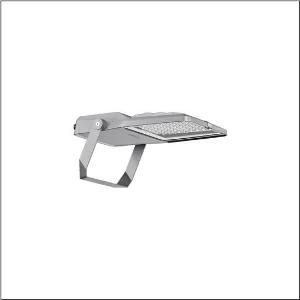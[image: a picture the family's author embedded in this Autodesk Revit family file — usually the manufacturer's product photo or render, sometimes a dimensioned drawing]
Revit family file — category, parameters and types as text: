
# Revit family: floodlight_fl_21_iq_mini___pl52_5xa7772c3d1a_c98d
name_source: partatom
category: Lighting Fixtures
units: mm (PartAtom-declared; Revit-internal decimal feet)

## family parameters
Cut with Voids When Loaded = No
Host = Face
Light Source = No
Part Type = Normal
Room Calculation Point = No
Round Connector Dimension = Use Diameter
Shared = No

## types (1)
- --- (1 x LED, 10510 lm, 87.2 W, 3000K)
    Apparent Load = 87 VA
    CIE Flux Codes = 26 60 98 100 100
    Color Rendering = 80
    Color Temperature = 3000K
    Default Elevation = 1800 mm
    Description = Floodlight FL 21 iQ mini, floodlight, primary light control with lens, of PMMA, primary optical cover: protective disc, of toughened safety glass, transparent, light distribution: PL52, light emission: direct distribution, installation type: surface-mounted, lamps: LED, High Power LED, rated values: 10.510lm | 87,2W | 120,5lm/W (begin service life); end service life: 10.510lm | 92,1W; at 50% lumin. flux: 5.255lm | 40,1W | 131lm/W, colour temperature: 3000K, colour rendering: CRI > 80, light colour: 830, light setting 1 begin service life: 100% | 10.510lm | 87,2W | 120,5lm/W | 3.000K, light setting 1 end service life: 92,1W, further light settings possible, control: Street-Remote, Auto-Match, Temp-Guard, Night-Set, Smart-Wire, Desk-Remote (wireless, voltage-free reading and setting of iQ features in the workshop via application-optimized NFC function/RFID function), optimised constant luminous flux control (CLO 2.0), pre-setting: linear dimming characteristic, with terminal, 6-pole, mains connection: 220..240V, AC, 50/60Hz, luminaire housing, of diecast aluminium, powder-coated, SITECO metallic grey (DB 702S), corrosivity category C5 mid according to DIN EN ISO 12944suitable for swimming poolschlorine-resistant, sealing non-destructively replaceable, mounting bracket, of steel, galvanised, powder-coated, SITECO metallic grey (DB 702S), protection rating (complete): IP66, insulation class (complete): insulation class II (safety insulation), certification: CE, ENEC, VDE, protection symbol: D, impact resistance: IK08, permissible operating ambient temperature: -40..+40°C, permissible operating ambient temperature for outdoor applications: -40..+50°C, standard: DIN EN 12944, LABS conformity tested according to VDMA 24364:2018-05, packaging unit: 1 piece

Light Distribution: PL52
    Height = 70 mm
    Lamp = 1 x LED
    Lamp Light Flux = 10510 lm
    Lamp Power = 87.2 W
    Lamp count = 1
    Length = 485 mm
    Luminous efficacy = 121 lm/W
    Manufacturer = Siteco
    ModVariant = No
    Model = 5XA7772C3D1A
    Mounting Place = Pole
    Mounting Type = Pole annexe
    Number of Poles = 1
    OnlyDefault = Yes
    Power Factor = 1
    Product Name = Floodlight FL 21 iQ mini | PL52
    Product group = floodlight | pylon annexe
    ProductGroupID = 6201
    Protection Class = Protection class II
    Protection Degree = IP 66
    RLX_Detail_Level = 1
    RLX_Emergency_Light_Flux = 0 lm
    RLX_Emergency_Type = 0
    RLX_Emergency_Type_DB = No
    RlxData = <blob elided: 96641 chars, md5=62e6d2f8>
    Socket = socket
    Standby Power = 0 W
    System Light Flux = 10510 lm
    System Power = 87 W
    Type Comments = factory setting: luminous flux: 100 % | dim-lin: 254 | 456 mA
    Type Image = l_1006845.jpg
    URL = http://relux.com
    VarID = @adj_165293
    Voltage = 0 V
    Weight = 0.00 kg
    Width = 337 mm

## geometry (parser evidence)
native form markers: Blend x4, Sweep x11
no freeform markers — native parametric forms only
